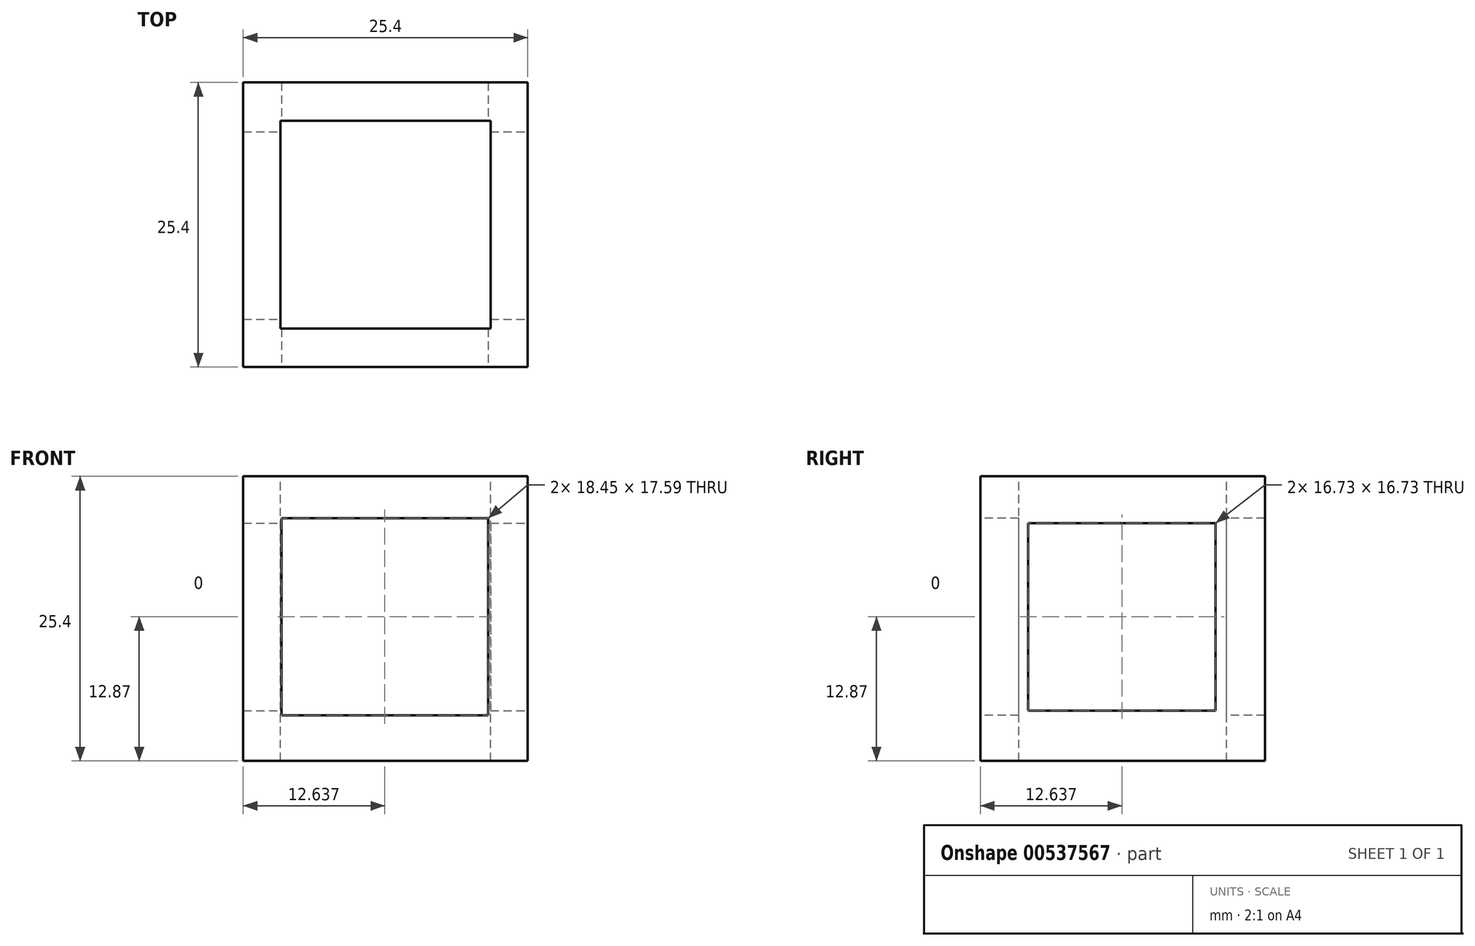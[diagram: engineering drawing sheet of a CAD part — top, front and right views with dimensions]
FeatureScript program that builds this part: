
annotation { "Feature Type Name" : "Feature", "Feature Type Description" : "" }
export const myFeature = defineFeature(function(context is Context, id is Id, definition is map)
    precondition{}
    {
        {
            var Q0;
            Q0=qCreatedBy(makeId("Front.planeOp"),FACE);
            var sketch = newSketch(context, id + "F0", { "sketchPlane" : qUnion([Q0])});
            skLineSegment(sketch, "E0", {"start": v(0, 0) * mm, "end": v(-25.4, 0) * mm});
            skLineSegment(sketch, "E1", {"start": v(-25.4, 0) * mm, "end": v(-25.4, 25.4) * mm});
            skLineSegment(sketch, "E2", {"start": v(-25.4, 25.4) * mm, "end": v(0, 25.4) * mm});
            skLineSegment(sketch, "E3", {"start": v(-1.8, 25.4) * mm, "end": v(0, 25.4) * mm});
            skLineSegment(sketch, "E4", {"start": v(0, 0) * mm, "end": v(0, 25.4) * mm});
            skSolve(sketch);
        }
        {
            var Q0;
            Q0=makeQuery(id+"F0.imprint","IMPRINT",FACE,{"disambiguationData":[TD([[makeQuery(id+"F0.imprint","IMPRINT",EDGE,{"derivedFrom":sQuery(id+"F0.wireOp",EDGE,"E0")}),-1.0]])]});
            extrude(context, id + "F1", {"entities" : qUnion([Q0]), "depth" : 25.4 * mm, "offsetDistance" : 25.4 * mm});
        }
        {
            var Q0;
            Q0=makeQuery(id+"F1.opExtrude","CAP_FACE",FACE,{"disambiguationData":[OSD([sQuery(id+"F0.wireOp",EDGE,"E0"),sQuery(id+"F0.wireOp",EDGE,"E1"),sQuery(id+"F0.wireOp",EDGE,"E2"),sQuery(id+"F0.wireOp",EDGE,"E3"),sQuery(id+"F0.wireOp",EDGE,"E4")])],"isStart":false});
            var sketch = newSketch(context, id + "F2", { "sketchPlane" : qUnion([Q0])});
            skPoint(sketch, "E5.middle", {"position": v(-12.76, 12.87) * mm});
            skPoint(sketch, "E5.left.start.orphan", {"position": v(-3.54, 21.66) * mm});
            skPoint(sketch, "E5.top.start.orphan", {"position": v(-3.54, 4.08) * mm});
            skPoint(sketch, "E5.right.end.orphan", {"position": v(-21.99, 4.08) * mm});
            skPoint(sketch, "E5.right.start.orphan", {"position": v(-21.99, 21.66) * mm});
            skLineSegment(sketch, "E6.bottom", {"start": v(-21.99, 4.08) * mm, "end": v(-3.54, 4.08) * mm});
            skLineSegment(sketch, "E6.top", {"start": v(-21.99, 21.66) * mm, "end": v(-3.54, 21.66) * mm});
            skLineSegment(sketch, "E6.left", {"start": v(-21.99, 4.08) * mm, "end": v(-21.99, 21.66) * mm});
            skLineSegment(sketch, "E6.right", {"start": v(-3.54, 4.08) * mm, "end": v(-3.54, 21.66) * mm});
            skSolve(sketch);
        }
        {
            var Q0;
            Q0 = qSketchRegion(id + "F2", true);
            extrude(context, id + "F3", {"entities" : qUnion([Q0]), "operationType" : NewBodyOperationType.REMOVE, "oppositeDirection" : true, "depth" : 25.4 * mm, "offsetDistance" : 25.4 * mm});
        }
        {
            var Q0;
            Q0=makeQuery(id+"F1.opExtrude","SWEPT_FACE",FACE,{"disambiguationData":[OSD([sQuery(id+"F0.wireOp",EDGE,"E4")])]});
            var sketch = newSketch(context, id + "F4", { "sketchPlane" : qUnion([Q0])});
            skLineSegment(sketch, "E7.bottom", {"start": v(-4.4, 21.24) * mm, "end": v(-21.13, 21.24) * mm});
            skLineSegment(sketch, "E7.top", {"start": v(-4.4, 4.5) * mm, "end": v(-21.13, 4.5) * mm});
            skLineSegment(sketch, "E7.left", {"start": v(-4.4, 21.24) * mm, "end": v(-4.4, 4.5) * mm});
            skLineSegment(sketch, "E7.right", {"start": v(-21.13, 21.24) * mm, "end": v(-21.13, 4.5) * mm});
            skPoint(sketch, "E7.middle", {"position": v(-12.76, 12.87) * mm});
            skSolve(sketch);
        }
        {
            var Q0;
            Q0 = qSketchRegion(id + "F4", true);
            extrude(context, id + "F5", {"entities" : qUnion([Q0]), "operationType" : NewBodyOperationType.REMOVE, "oppositeDirection" : true, "depth" : 25.4 * mm, "offsetDistance" : 25.4 * mm});
        }
        {
            var Q0;
            Q0=makeQuery(id+"F1.opExtrude","SWEPT_FACE",FACE,{"disambiguationData":[OSD([sQuery(id+"F0.wireOp",EDGE,"E2"),sQuery(id+"F0.wireOp",EDGE,"E3")])]});
            var sketch = newSketch(context, id + "F6", { "sketchPlane" : qUnion([Q0])});
            skLineSegment(sketch, "E8.bottom", {"start": v(-3.32, -3.43) * mm, "end": v(-22.08, -3.43) * mm});
            skLineSegment(sketch, "E8.top", {"start": v(-3.32, -21.97) * mm, "end": v(-22.08, -21.97) * mm});
            skLineSegment(sketch, "E8.left", {"start": v(-3.32, -3.43) * mm, "end": v(-3.32, -21.97) * mm});
            skLineSegment(sketch, "E8.right", {"start": v(-22.08, -3.43) * mm, "end": v(-22.08, -21.97) * mm});
            skPoint(sketch, "E8.middle", {"position": v(-12.7, -12.7) * mm});
            skPoint(sketch, "E8.middle.positionSnap0", {"position": v(0, -12.7) * mm});
            skPoint(sketch, "E8.middle.positionSnap1", {"position": v(-12.7, 0) * mm});
            skPoint(sketch, "E8.centerSnap0", {"position": v(0, -12.7) * mm});
            skPoint(sketch, "E8.centerSnap1", {"position": v(-12.7, 0) * mm});
            skSolve(sketch);
        }
        {
            var Q0;
            Q0 = qSketchRegion(id + "F6", true);
            extrude(context, id + "F7", {"entities" : qUnion([Q0]), "operationType" : NewBodyOperationType.REMOVE, "oppositeDirection" : true, "depth" : 25.4 * mm, "offsetDistance" : 25.4 * mm});
        }
    });
